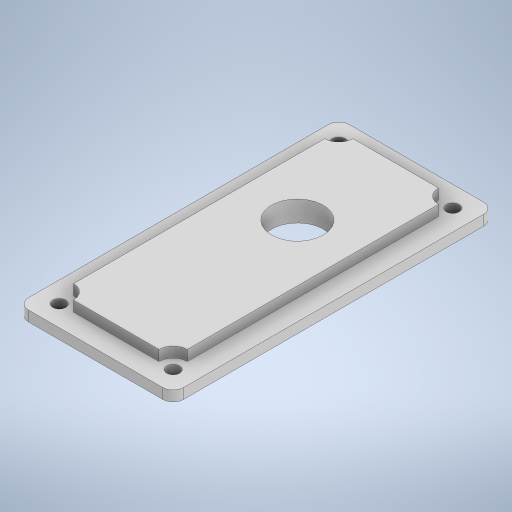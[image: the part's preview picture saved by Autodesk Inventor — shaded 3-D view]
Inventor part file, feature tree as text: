
AUTODESK INVENTOR PART (.ipt)
format: ipt  version: 2023.1 (Build 271208000, 208)  size: 269,824 bytes
history: native  units: mm
features: extrude x3, sketch x2, other x1, fillet x1
ambient origin geometry x8: Origin, YZ Plane, XZ Plane, XY Plane, X Axis, Y Axis, Z Axis, Center Point
bodies: Body1 (feature_tree)
feature tree (7):
  other  "솔리드1"
  sketch  "스케치1"
  extrude  "돌출1"  Depth=22.0mm
  extrude  "돌출2"  Depth=54.0mm
  fillet  "모깎기1"  Radius=4.0mm
  extrude  "돌출3"  Depth=2.5mm
  sketch  "스케치2"
